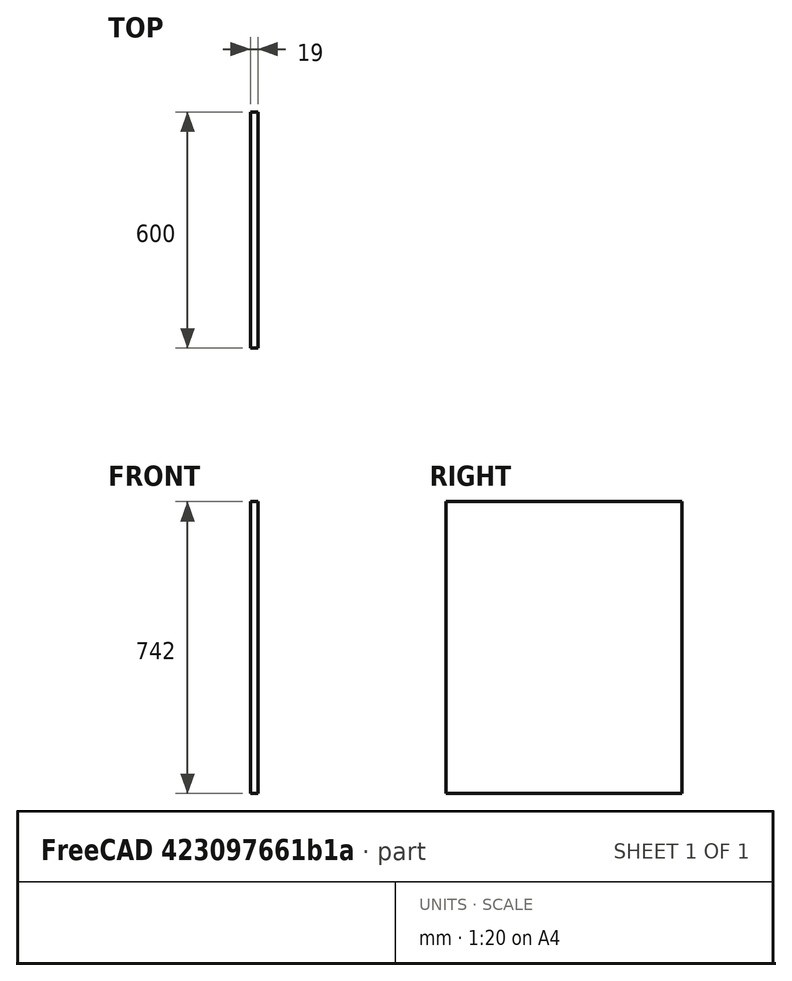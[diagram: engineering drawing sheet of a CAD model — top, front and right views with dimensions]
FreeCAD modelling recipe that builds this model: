
FCSTD DOCUMENT  (FreeCAD 1.0RUnknown)
Label: wardrobe_left_corpus02_jan
License: All rights reserved
LicenseURL: https://en.wikipedia.org/wiki/All_rights_reserved
objects: PartDesign::CoordinateSystem×3, Sketcher::SketchObject×1, PartDesign::Pad×1, PartDesign::Body×1
note: 9 computed .brp shape members not serialized (recipe doc carries the construction recipe); baked Part::Feature solids carry a one-line shape summary decoded from their .brp
EXTERNAL_REF file=../../mastersketch.FCStd obj=Spreadsheet

FEATURE [Sketcher::SketchObject] Sketch001
  ArcFitTolerance = 1e-06
  AttachmentSupport = -> [YZ_Plane001]
  FullyConstrained = true
  MakeInternals = false
  MapMode = 5
  Placement = pos=(0,0,0) rot=(0.57735,0.57735,0.57735;2.0944rad)
  expr: Constraints[10] = mastersketch#Spreadsheet.corpus_depth
  expr: Constraints[11] = mastersketch#Spreadsheet.corpus02_height - 2 * mastersketch#Spreadsheet.corpus_outer_thickness
  sketch-geometry (5):
    g0: LineSegment StartX=-300 StartY=-371 StartZ=0 EndX=300 EndY=-371 EndZ=0
    g1: LineSegment StartX=300 StartY=-371 StartZ=0 EndX=300 EndY=371 EndZ=0
    g2: LineSegment StartX=300 StartY=371 StartZ=0 EndX=-300 EndY=371 EndZ=0
    g3: LineSegment StartX=-300 StartY=371 StartZ=0 EndX=-300 EndY=-371 EndZ=0
    g4: GeomPoint [constr] X=0 Y=0 Z=0
  constraints (12):
    c: Coincident(g0,g1)
    c: Coincident(g1,g2)
    c: Coincident(g2,g3)
    c: Coincident(g3,g0)
    c: Horizontal(g0)
    c: Horizontal(g2)
    c: Vertical(g1)
    c: Vertical(g3)
    c: Symmetric(g2,g0,g4)
    c: Coincident(g4,g-1)
    c: DistanceX(g0,g0) = 600
    c: DistanceY(g3,g3) = 742
FEATURE [PartDesign::Pad] Pad001
  Direction = (1,0,0)
  Length = 19
  Length2 = 10
  Placement = pos=(0,0,0) rot=(1,1,1;2.0944rad)
  Profile = -> Sketch001
  ReferenceAxis = -> Sketch001 [N_Axis]
  Refine = true
  Suppressed = false
  Type = 0
  expr: Length = mastersketch#Spreadsheet.corpus_outer_thickness
FEATURE [PartDesign::CoordinateSystem] LCS_1  label="LCS_bottom"
  AttacherType = Attacher::AttachEngine3D
  AttachmentSupport = -> [Pad001]
  MapMode = 45
  Placement = pos=(0,-1.42e-14,-371) rot=(0,0.707107,0.707107;3.14159rad)
FEATURE [PartDesign::CoordinateSystem] LCS_top
  AttacherType = Attacher::AttachEngine3D
  AttachmentSupport = -> [Pad001]
  MapMode = 45
  Placement = pos=(0,1.42e-14,371) rot=(0,0.707107,0.707107;3.14159rad)
FEATURE [PartDesign::CoordinateSystem] LCS_inner
  AttacherType = Attacher::AttachEngine3D
  AttachmentSupport = -> [Pad001]
  MapMode = 45
  Placement = pos=(19,-1.82e-14,-371) rot=(0,0.707107,0.707107;3.14159rad)
FEATURE [PartDesign::Body] Body001  label="wardrobe_left_corpus02_jan"
  AllowCompound = false
  Group = -> [Sketch001,Pad001,LCS_1,LCS_top,LCS_inner]
  Origin = -> Origin001
  Tip = -> Pad001
